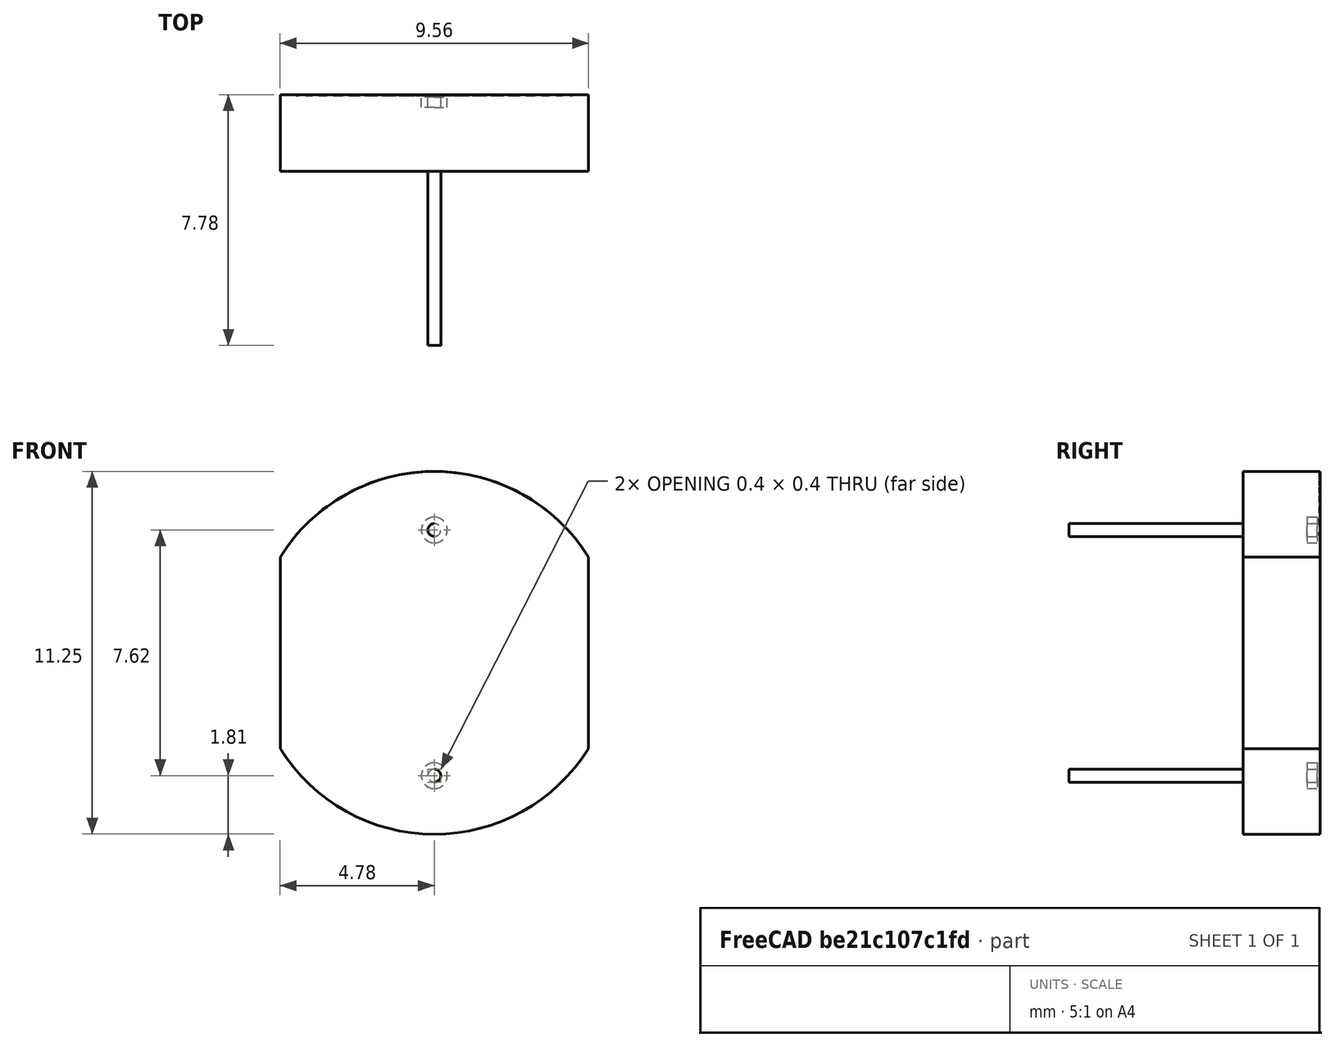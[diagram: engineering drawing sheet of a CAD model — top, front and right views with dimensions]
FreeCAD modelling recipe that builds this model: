
FCSTD DOCUMENT  (FreeCAD 0.16R5239 (Git))
Label: LDR
License: All rights reserved
LicenseURL: http://en.wikipedia.org/wiki/All_rights_reserved
objects: Part::Feature×5, Part::FeaturePython×2, Part::MultiFuse×1
note: 8 computed .brp shape members not serialized (recipe doc carries the construction recipe); baked Part::Feature solids carry a one-line shape summary decoded from their .brp

FEATURE [Part::Feature] Part__Feature  label="User Library-PDV-P5001_1_1"
  shape: bbox 8.571 x 0.01 x 9.647 mm, 719 faces (baked)
FEATURE [Part::Feature] Part__Feature001  label="User Library-PDV-P5001_2_1"
  shape: bbox 0.8 x 38.88 x 0.8 mm, 7 faces (baked)
FEATURE [Part::Feature] Part__Feature002  label="User Library-PDV-P5001_3_1"
  shape: bbox 9.555 x 2.385 x 11.25 mm, 735 faces (baked)
FEATURE [Part::Feature] Part__Feature003  label="User Library-PDV-P5001_4_1"
  shape: bbox 0.8 x 38.88 x 0.8 mm, 7 faces (baked)
FEATURE [Part::FeaturePython] Clone  label="Clone of User Library-PDV-P5001_2_1"  # Draft clone (typed FeaturePython)
  Objects = -> [Part__Feature001]
  Placement = pos=(0,15.55,0) rot=(0,0,1;0rad)
  Scale = (1,0.2,1)
FEATURE [Part::FeaturePython] Clone001  label="Clone of User Library-PDV-P5001_4_1"  # Draft clone (typed FeaturePython)
  Objects = -> [Part__Feature003]
  Placement = pos=(0,15.55,0) rot=(0,0,1;0rad)
  Scale = (1,0.2,1)
FEATURE [Part::MultiFuse] Fusion
  Shapes = -> [Part__Feature,Part__Feature002,Clone,Clone001]
FEATURE [Part::Feature] Fusion001
  shape: bbox 9.555 x 7.783 x 11.25 mm, 86 faces (baked)
